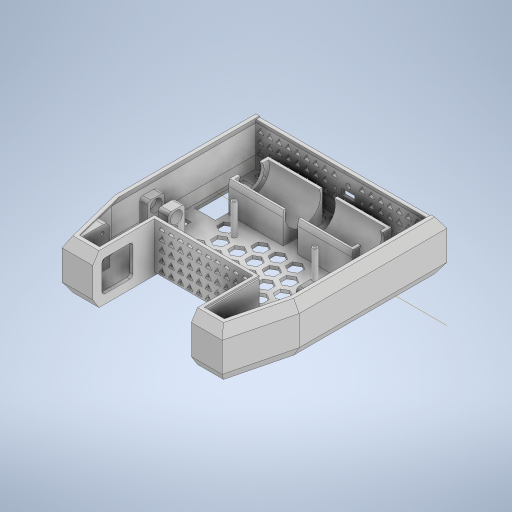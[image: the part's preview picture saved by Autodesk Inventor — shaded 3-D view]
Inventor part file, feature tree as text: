
AUTODESK INVENTOR PART (.ipt)
format: ipt  version: 2024 (Build 280153000, 153)  size: 3,643,904 bytes
history: native  units: in
note: dims shown in document units (in); Inventor stores cm internally (conversion verified against a paired STEP export)
features: projected_geometry x36, extrude x35, sketch x32, fillet x8, chamfer x6, plane x3, mirror x2, shell x1, other x1, hole x1
ambient origin geometry x8: Origin, YZ Plane, XZ Plane, XY Plane, X Axis, Y Axis, Z Axis, Center Point
bodies: Solid1 (feature_tree)
feature tree (125):
  extrude  "Extrusion1"  Depth=1.25in
  chamfer  "Chamfer1"  Distance=2.0in
  chamfer  "Chamfer2"  Distance=0.25in Angle=30.0deg
  shell  "Shell1"  Thickness=0.125in
  extrude  "Extrusion2"  Depth=2.0in
  extrude  "Extrusion3"  Depth=0.125in
  sketch  "Sketch4"  dims[d17=2.0in d18=0.125in]
  extrude  "Extrusion4"  Depth=0.425in
  extrude  "Extrusion5"  Depth=0.125in
  other  "Work Axis1"
  extrude  "Extrusion6"  Depth=0.125in
  plane  "Work Plane1"
  extrude  "Extrusion7"  Depth=0.0625in
  extrude  "Extrusion8"  Depth=0.0625in
  mirror  "Mirror1"
  extrude  "Extrusion12"  Depth=0.0625in TaperAngle=0.0deg
  fillet  "Fillet1"  Radius=1.6in
  extrude  "Extrusion13"  Depth=0.2in
  sketch  "Sketch15"  dims[d38=2.08in d39=0.2in]
  extrude  "Extrusion14"  Depth=1.25in
  fillet  "Fillet2"  [1 undecoded]
  extrude  "Extrusion15"  Depth=1.0in
  fillet  "Fillet3"  Radius=1.45in
  sketch  "Sketch16"  dims[d40=0.268in d41=1.25in d42=0.0in]
  hole  "Hole1"  [1 undecoded]
  extrude  "Extrusion16"  Depth=0.125in TaperAngle=0.0deg
  extrude  "Extrusion17"  Depth=1.0in
  plane  "Work Plane3"
  sketch  "Sketch18"  dims[d51=0.09in d52=0.07in]
  extrude  "Extrusion18"  TaperAngle=45.0deg  [1 undecoded]
  extrude  "Extrusion19"  Depth=1.5748in TaperAngle=360.0deg
  extrude  "Extrusion20"  Depth=1.0in
  extrude  "Extrusion21"  Depth=1.76in
  mirror  "Mirror2"
  extrude  "Extrusion22"  Depth=0.125in
  chamfer  "Chamfer4"  Distance=0.8661in
  extrude  "Extrusion23"  Depth=0.5in
  chamfer  "Chamfer5"  Distance=0.125in
  chamfer  "Chamfer6"  Distance=1.0in
  chamfer  "Chamfer7"  Distance=0.125in
  extrude  "Extrusion24"  Depth=0.125in
  fillet  "Fillet4"  Radius=0.125in
  plane  "Work Plane4"
  extrude  "Extrusion26"  Depth=0.5in
  extrude  "Extrusion27"  Depth=0.475in
  extrude  "Extrusion28"  Depth=0.25in
  extrude  "Extrusion29"  Depth=1.0in TaperAngle=0.0deg
  extrude  "Extrusion30"  Depth=0.455in
  extrude  "Extrusion31"  Depth=0.555in
  fillet  "Fillet5"  Radius=1.0in
  fillet  "Fillet6"  Radius=1.0in
  extrude  "Extrusion32"  Depth=0.69in
  extrude  "Extrusion33"  Depth=0.345in
  extrude  "Extrusion34"  Depth=1.0in TaperAngle=0.0deg
  fillet  "Fillet7"  Radius=0.4in
  fillet  "Fillet8"  Radius=0.3in
  extrude  "Cutouts1"  Depth=0.5in
  extrude  "Cutouts2"  Depth=1.05in TaperAngle=0.0deg
  extrude  "Cutouts3"  Depth=0.12in
  extrude  "Cutouts4"  Depth=0.35in
  extrude  "Extrusion9"  Depth=1.05in TaperAngle=0.0deg
  sketch  "Sketch1"  dims[d4=1.25in d5=1.25in d6=2.0in d7=0.0in d8=0.25in d9=0.4in d10=30.0deg]
  sketch  "Sketch2"  dims[d11=0.25in d12=0.4in d13=60.0deg d14=0.125in]
  projected_geometry  "Projected Loop1"
  sketch  "Sketch3"  dims[d15=0.85in d16=2.0in]
  projected_geometry  "Projected Loop2"
  projected_geometry  "Projected Loop3"
  projected_geometry  "Projected Loop4"
  sketch  "Sketch5"  dims[d19=0.125in d21=0.425in]
  sketch  "Sketch6"  dims[d22=1.0in d23=0.0in d24=0.125in]
  projected_geometry  "Projected Loop5"
  sketch  "Sketch7"  dims[d25=0.125in d26=0.125in]
  projected_geometry  "Projected Loop6"
  sketch  "Sketch8"  dims[d27=1.0in d28=0.0in d29=0.0625in]
  projected_geometry  "Projected Loop7"
  sketch  "Sketch12"  dims[d30=0.0625in d31=0.0625in]
  projected_geometry  "Projected Loop13"
  projected_geometry  "Projected Loop14"
  sketch  "Sketch13"  dims[d32=0.0625in d33=0.0in d34=0.0625in d35=0.0in d36=1.6in]
  projected_geometry  "Projected Loop15"
  projected_geometry  "Projected Loop17"
  projected_geometry  "Projected Loop18"
  sketch  "Sketch17"  dims[d44=5.6in d45=0.0in d46=1.0in d47=1.45in]
  projected_geometry  "Projected Loop19"
  projected_geometry  "Projected Loop20"
  projected_geometry  "Projected Loop21"
  sketch  "Sketch19"  dims[d53=2.3622in d55=360.0deg d57=0.125in d58=0.0in]
  sketch  "Sketch21"  dims[d60=1.0in d61=1.0336in]
  projected_geometry  "Projected Loop23"
  projected_geometry  "Projected Loop24"
  projected_geometry  "Projected Loop25"
  sketch  "Sketch22"  dims[d62=0.31in d63=45.0deg]
  sketch  "Sketch23"  dims[d64=0.6425in d65=1.5748in d67=360.0deg]
  sketch  "Sketch24"  dims[d69=1.0in d70=0.0in d80=1.3124in]
  projected_geometry  "Projected Loop26"
  sketch  "Sketch26"  dims[d81=1.0in d83=1.76in]
  projected_geometry  "Projected Loop28"
  projected_geometry  "Projected Loop29"
  projected_geometry  "Projected Loop30"
  projected_geometry  "Projected Loop31"
  projected_geometry  "Projected Loop32"
  projected_geometry  "Projected Loop33"
  sketch  "Sketch27"  dims[d84=1.0in d85=0.0in d86=0.125in]
  projected_geometry  "Projected Loop34"
  sketch  "Sketch28"  dims[d87=0.34in]
  sketch  "Sketch29"  dims[d88=0.3in]
  sketch  "Sketch30"  dims[d89=0.1in]
  projected_geometry  "Projected Loop35"
  sketch  "Sketch31"  dims[d90=0.375in]
  projected_geometry  "Projected Loop36"
  sketch  "Sketch32"  dims[d93=0.005in]
  sketch  "Sketch33"  dims[d94=0.005in]
  sketch  "Sketch34"  dims[d95=0.005in]
  projected_geometry  "Projected Loop37"
  projected_geometry  "Projected Loop38"
  projected_geometry  "Projected Loop40"
  sketch  "Sketch36"  dims[d96=0.005in]
  projected_geometry  "Projected Loop41"
  sketch  "Sketch37"  dims[d97=0.005in]
  projected_geometry  "Projected Loop42"
  sketch  "Sketch39"  dims[d98=0.005in d99=0.8661in d100=0.0in]
  projected_geometry  "Projected Loop45"
  projected_geometry  "Projected Loop46"
  sketch  "Sketch40"  dims[d107=0.305in d108=0.305in d110=0.125in d113=1.0in d114=0.0in d115=0.125in d116=0.0in d117=0.125in d118=0.125in d122=0.801in d124=0.1575in d125=0.75in d126=0.417in d127=0.118in d128=90.0deg d129=0.125in d130=0.0in d131=0.475in d133=0.25in d134=1.0in d135=0.0in d136=0.455in d137=0.555in d138=1.0in d139=0.0in d140=1.0in d141=0.69in d143=0.345in d144=1.0in d145=0.0in d147=0.4in d148=0.3in d149=0.0in d150=0.49in d151=1.05in d152=0.0in d153=0.12in d154=0.35in d155=1.05in d156=0.0in d157=1.45in d158=0.21in d159=0.07in d160=0.12in d161=2.3622in d163=360.0deg d165=1.625in d166=1.375in d168=0.1in d169=0.05in d170=0.075in d171=0.025in d172=0.05in d173=0.0in d174=0.05in d175=0.1in d176=30.0deg d177=0.4in d178=0.05in d179=0.0in d180=0.15in d181=0.05in d182=30.0deg d183=0.15in d184=0.05in d185=30.0deg d186=0.15in d187=0.05in d188=30.0deg d189=1.26in d190=1.26in d191=0.05in d192=0.0in d193=0.125in d200=0.95in d201=1.5in d202=0.125in d203=0.125in d204=0.125in d205=0.125in d206=0.447in d207=0.0in d208=0.9087in d209=0.9087in d210=0.4543in d211=0.4543in d212=0.1575in d213=0.1772in d214=0.0in d215=0.125in d216=0.125in d217=0.1772in d218=0.0in d219=0.9in d220=0.125in d221=0.8in d222=0.125in d224=0.125in d225=0.5in d226=0.45in d227=2.78in d228=0.8in d229=0.0in d230=0.125in d231=0.125in d232=0.8in d233=0.0in d234=0.125in d235=0.125in d236=0.25in d237=1.0in d238=0.0in d239=0.125in d240=0.0625in d241=0.2in d242=3.285in d243=2.555in d244=0.2in d246=1.25in d247=0.0in d248=0.52in d249=0.26in d250=0.2in d251=0.2in d252=0.25in d253=0.75in d254=0.15in d255=1.25in d256=0.1in d257=0.0in d260=0.0in d261=0.125in d262=0.125in d263=0.125in d264=0.125in d265=1.0in d266=0.0in d307=1.6425in d309=0.5in d310=0.5in d311=0.2in d312=0.5in d313=0.2in d314=0.2in d315=0.5in d316=0.2in d317=0.2in d318=0.2in d319=0.7874in d321=1.4in d322=1.1811in d324=1.2in d327=1.1811in d329=0.7in d330=0.3937in d332=1.0in d334=0.5in d335=0.5in d336=0.5in d337=0.2in d338=0.2in d339=0.2in d340=0.2in d341=0.2in d342=0.2in d343=1.0in d344=0.0in d345=0.2785in d347=0.125in d349=0.1in d350=0.1in d351=5.1181in d353=0.5in d354=0.3937in d356=1.0in d359=0.25in d360=0.25in d361=0.0in d362=0.0in d363=0.125in d364=0.125in d369=60.0deg d370=0.25in d371=3.937in d373=0.375in d374=1.9685in d376=0.375in d379=0.0625in d380=0.08in d381=1.0in d382=0.0in d383=0.0625in d384=0.25in d385=60.0deg d386=7.874in d388=0.375in d389=1.1811in d391=0.375in d394=0.1in d395=0.0625in d396=1.0in d397=0.0in d398=0.5in d399=0.0344in d400=0.5in d401=0.0344in]
  projected_geometry  "Projected Loop47"
note: 3 required parameter values undecoded (feature->parameter linkage not recoverable at this tier; creation-order binding heuristic only, values carry confidence <= 0.55)
